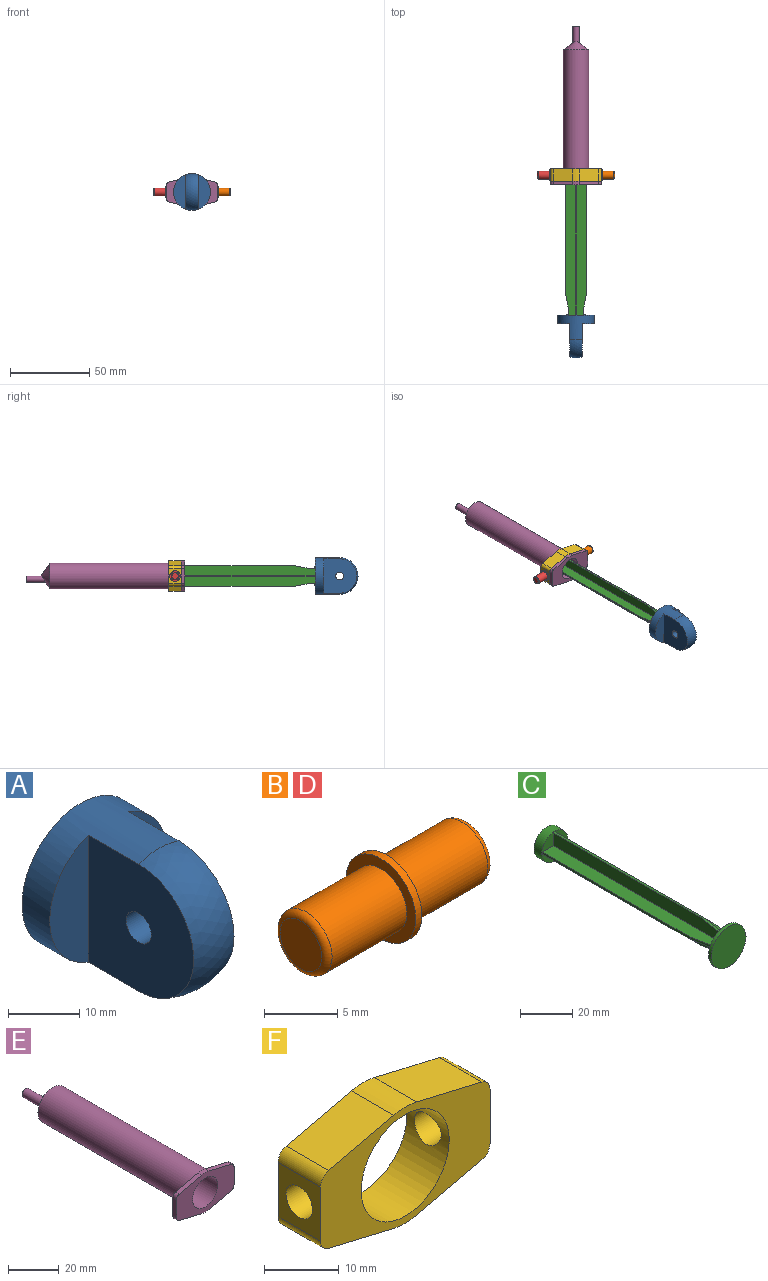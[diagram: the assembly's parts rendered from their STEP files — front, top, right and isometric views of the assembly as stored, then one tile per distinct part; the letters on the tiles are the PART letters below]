
ASSEMBLY  parts=6 mates=5
PART A: 10 faces, bbox 23.2x27.1x23.2 mm
  f0: plane 21.78x7.6mm, normal (0,-1,0), area 120.4mm2, adj f4,f7
  f1: plane 19.2x19.2mm, normal (0,1,0), area 289.5mm2, adj f2
  f2: cylinder r=9.6mm len=19.2mm, axis (0,-1,0), area 90.5mm2, adj f1,f3
  f3: plane 23.2x23.2mm, normal (0,1,0), area 133.2mm2, adj f2,f4
  f4: cylinder r=11.6mm len=23.2mm, axis (0,-1,0), area 564.2mm2, adj f0,f3,f5,f6,f7,f8
  f5: plane 21.78x7.6mm, normal (0,-1,0), area 120.4mm2, adj f4,f6
  f6: plane 21.78x20.89mm, normal (-1,0,0), area 384.4mm2, adj f4,f5,f8,f9
  f7: plane 21.78x20.89mm, normal (1,0,0), area 384.4mm2, adj f0,f4,f8,f9
  f8: sphere r=11.6mm, area 291.5mm2, adj f4,f6,f7
  f9: cylinder r=2.5mm len=8mm, axis (-1,0,0), area 125.7mm2, adj f6,f7
PART B: 9 faces, bbox 16x6.7x6.7 mm
  f0: cylinder r=2.5mm len=7.2mm, axis (-1,0,0), area 113.1mm2, adj f6,f7
  f1: plane 4x4mm, normal (-1,0,0), area 12.6mm2, adj f7
  f2: plane 4x4mm, normal (1,0,0), area 12.6mm2, adj f8
  f3: cylinder r=2.5mm len=7.2mm, axis (-1,0,0), area 113.1mm2, adj f4,f8
  f4: plane 6.7x6.7mm, normal (1,0,0), area 15.6mm2, adj f3,f5
  f5: cylinder r=3.35mm len=6.7mm, axis (-1,0,0), area 12.6mm2, adj f4,f6
  f6: plane 6.7x6.7mm, normal (-1,0,0), area 15.6mm2, adj f0,f5
  f7: torus R=2mm, axis (1,0,0), area 11.4mm2, adj f0,f1
  f8: torus R=2mm, axis (-1,0,0), area 11.4mm2, adj f2,f3
PART C: 26 faces, bbox 18.8x103.5x18.8 mm
  f0: plane 14x14mm, normal (0,-1,0), area 128.9mm2, adj f2,f3,f6,f7,f8,f9,f12,f13
  f1: cone r=0mm half-angle=55.8deg, axis (0,-1,0), area 186.1mm2, adj f2
  f2: cylinder r=7mm len=14mm, axis (0,-1,0), area 186.8mm2, adj f0,f1
  f3: plane 80x1mm, normal (0,0,1), area 80mm2, adj f0,f4,f6,f7
  f4: plane 10.64x1.97mm, normal (0,-0.18,0.98), area 10.8mm2, adj f3,f5,f6,f7
  f5: cylinder r=2mm len=2.36mm, axis (-1,0,0), area 3.5mm2, adj f4,f6,f7,f23
  f6: plane 93x6mm, normal (1,0,0), area 543.7mm2, adj f0,f3,f4,f5,f12,f23
  f7: plane 93x6mm, normal (-1,0,0), area 543.7mm2, adj f0,f3,f4,f5,f8,f23
  f8: plane 93x6mm, normal (0,0,1), area 543.7mm2, adj f0,f7,f9,f10,f11,f23
  f9: plane 80x1mm, normal (-1,0,0), area 80mm2, adj f0,f8,f10,f13
  f10: plane 10.64x1.97mm, normal (-0.98,-0.18,0), area 10.8mm2, adj f8,f9,f11,f13
  f11: cylinder r=2mm len=2.36mm, axis (0,0,-1), area 3.5mm2, adj f8,f10,f13,f23
  f12: plane 93x6mm, normal (0,0,1), area 543.7mm2, adj f0,f6,f20,f21,f22,f23
  f13: plane 93x6mm, normal (0,0,-1), area 543.7mm2, adj f0,f9,f10,f11,f14,f23
  f14: plane 93x6mm, normal (-1,0,0), area 543.7mm2, adj f0,f13,f15,f16,f17,f23
  f15: plane 80x1mm, normal (0,0,-1), area 80mm2, adj f0,f14,f16,f18
  f16: plane 10.64x1.97mm, normal (0,-0.18,-0.98), area 10.8mm2, adj f14,f15,f17,f18
  f17: cylinder r=2mm len=2.36mm, axis (1,0,0), area 3.5mm2, adj f14,f16,f18,f23
  f18: plane 93x6mm, normal (1,0,0), area 543.7mm2, adj f0,f15,f16,f17,f19,f23
  f19: plane 93x6mm, normal (0,0,-1), area 543.7mm2, adj f0,f18,f20,f21,f22,f23
  f20: plane 80x1mm, normal (1,0,0), area 80mm2, adj f0,f12,f19,f21
  f21: plane 10.64x1.97mm, normal (0.98,-0.18,0), area 10.8mm2, adj f12,f19,f20,f22
  f22: cylinder r=2mm len=2.36mm, axis (0,0,1), area 3.5mm2, adj f12,f19,f21,f23
  f23: plane 18.8x18.8mm, normal (0,1,0), area 252.6mm2, adj f5,f6,f7,f8,f11,f12,f13,f14
  f24: cylinder r=9.4mm len=18.8mm, axis (0,1,0), area 88.6mm2, adj f23,f25
  f25: plane 18.8x18.8mm, normal (0,-1,0), area 277.6mm2, adj f24
PART D: same geometry as B
PART E: 22 faces, bbox 32x100x19 mm
  f0: cone r=7mm half-angle=55.8deg, axis (0,-1,0), area 182.3mm2, adj f1,f18
  f1: cylinder r=7mm len=85mm, axis (0,-1,0), area 3738.5mm2, adj f0,f2
  f2: plane 32x19mm, normal (0,-1,0), area 347.6mm2, adj f1,f3,f7,f8,f9,f10,f11,f12
  f3: cylinder r=2mm len=2mm, axis (0,-1,0), area 5.4mm2, adj f2,f4,f7,f17
  f4: plane 32x19mm, normal (0,1,0), area 295.4mm2, adj f3,f5,f7,f8,f9,f10,f11,f12
  f5: cylinder r=8.1mm len=83mm, axis (0,-1,0), area 4224.2mm2, adj f4,f6
  f6: cone r=0mm half-angle=55.8deg, axis (0,-1,0), area 249.1mm2, adj f5
  f7: plane 8.83x2mm, normal (1,0,0), area 17.7mm2, adj f2,f3,f4,f8
  f8: cylinder r=2mm len=2mm, axis (0,-1,0), area 5.4mm2, adj f2,f4,f7,f9
  f9: plane 12.29x2.89mm, normal (0.23,0,-0.97), area 25.2mm2, adj f2,f4,f8,f10
  f10: cylinder r=9.5mm len=4.35mm, axis (0,-1,0), area 8.8mm2, adj f2,f4,f9,f11
  f11: plane 12.29x2.89mm, normal (-0.23,0,-0.97), area 25.2mm2, adj f2,f4,f10,f12
  f12: cylinder r=2mm len=2mm, axis (0,-1,0), area 5.4mm2, adj f2,f4,f11,f13
  f13: plane 8.83x2mm, normal (-1,0,0), area 17.7mm2, adj f2,f4,f12,f14
  f14: cylinder r=2mm len=2mm, axis (0,-1,0), area 5.4mm2, adj f2,f4,f13,f15
  f15: plane 12.29x2.89mm, normal (-0.23,0,0.97), area 25.2mm2, adj f2,f4,f14,f16
  f16: cylinder r=9.5mm len=4.35mm, axis (0,-1,0), area 8.8mm2, adj f2,f4,f15,f17
  f17: plane 12.29x2.89mm, normal (0.23,0,0.97), area 25.2mm2, adj f2,f3,f4,f16
  f18: cylinder r=1mm len=12.28mm, axis (0,1,0), area 73.4mm2, adj f0,f19
  f19: plane 4x4mm, normal (0,1,0), area 9.4mm2, adj f18,f20
  f20: cylinder r=2mm len=12.22mm, axis (0,1,0), area 141.1mm2, adj f19,f21
  f21: cone r=0mm half-angle=55.8deg, axis (0,-1,0), area 15.2mm2, adj f20
PART F: 17 faces, bbox 32x8x19 mm
  f0: plane 12.29x8mm, normal (0.23,0,-0.97), area 101mm2, adj f1,f12,f13,f14
  f1: cylinder r=9.5mm len=8mm, axis (0,-1,0), area 35.1mm2, adj f0,f2,f13,f14
  f2: plane 12.29x8mm, normal (-0.23,0,-0.97), area 101mm2, adj f1,f3,f13,f14
  f3: cylinder r=2mm len=8mm, axis (0,-1,0), area 21.4mm2, adj f2,f4,f13,f14
  f4: plane 8.83x8mm, normal (-1,0,0), area 51mm2, adj f3,f5,f13,f14,f16
  f5: cylinder r=2mm len=8mm, axis (0,-1,0), area 21.4mm2, adj f4,f6,f13,f14
  f6: plane 12.29x8mm, normal (-0.23,0,0.97), area 101mm2, adj f5,f7,f13,f14
  f7: cylinder r=9.5mm len=8mm, axis (0,-1,0), area 35.1mm2, adj f6,f8,f13,f14
  f8: plane 12.29x8mm, normal (0.23,0,0.97), area 101mm2, adj f7,f9,f13,f14
  f9: cylinder r=2mm len=8mm, axis (0,-1,0), area 21.4mm2, adj f8,f10,f13,f14
  f10: plane 8.83x8mm, normal (1,0,0), area 51mm2, adj f9,f12,f13,f14,f15
  f11: cylinder r=8.3mm len=16.6mm, axis (0,-1,0), area 377.4mm2, adj f13,f14,f15,f16
  f12: cylinder r=2mm len=8mm, axis (0,-1,0), area 21.4mm2, adj f0,f10,f13,f14
  f13: plane 32x19mm, normal (0,1,0), area 285.1mm2, adj f0,f1,f2,f3,f4,f5,f6,f7
  f14: plane 32x19mm, normal (0,-1,0), area 285.1mm2, adj f0,f1,f2,f3,f4,f5,f6,f7
  f15: cylinder r=2.5mm len=8.09mm, axis (1,0,0), area 124mm2, adj f10,f11
  f16: cylinder r=2.5mm len=8.09mm, axis (1,0,0), area 124mm2, adj f4,f11
PLACE A t=(3.17,-70,-4.12)mm
PLACE B t=(19.47,6,-4.12)mm
PLACE C rot(axis=(0,1,0),180deg) t=(3.17,-70,-4.12)mm
PLACE D t=(-13.13,6,-4.12)mm
PLACE E t=(3.17,0,-4.12)mm fixed
PLACE F t=(3.17,0,-4.12)mm
MATE fastened A.f2 <-> C.f24  axis (0,-1,0) through (3.17,-83.75,-4.12)mm
MATE fastened B.f0 <-> F.f15  axis (-1,0,0) through (19.17,6,-4.12)mm
MATE fastened D.f0 <-> F.f15  axis (-1,0,0) through (-12.83,6,-4.12)mm
MATE fastened E.f0 <-> F.f1  axis (0,1,0) through (3.17,2,-4.12)mm
MATE slider C.f2 <-> E.f0  axis (0,-1,0) through (3.17,15,-4.12)mm
